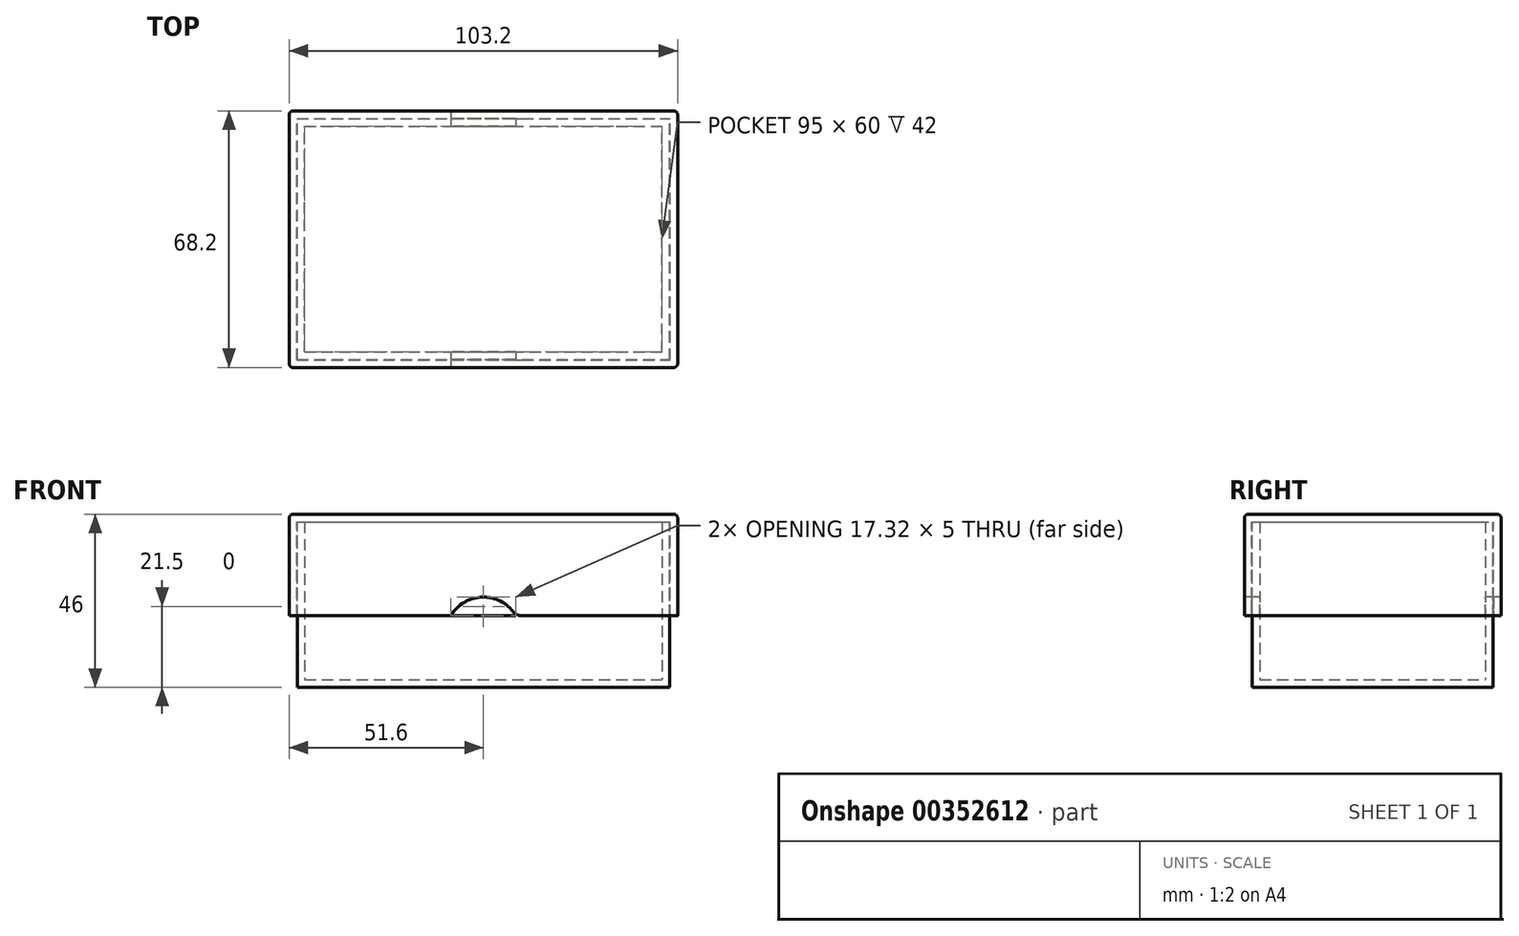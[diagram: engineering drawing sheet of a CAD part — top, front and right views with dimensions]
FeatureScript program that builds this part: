
annotation { "Feature Type Name" : "Feature", "Feature Type Description" : "" }
export const myFeature = defineFeature(function(context is Context, id is Id, definition is map)
    precondition{}
    {
        {
            var Q0;
            Q0=qCreatedBy(makeId("Top.planeOp"),FACE);
            var sketch = newSketch(context, id + "F0", { "sketchPlane" : qUnion([Q0])});
            skLineSegment(sketch, "E0.bottom", {"start": v(0, 0) * mm, "end": v(95, 0) * mm});
            skLineSegment(sketch, "E0.top", {"start": v(0, 60) * mm, "end": v(95, 60) * mm});
            skLineSegment(sketch, "E0.left", {"start": v(0, 0) * mm, "end": v(0, 60) * mm});
            skLineSegment(sketch, "E0.right", {"start": v(95, 0) * mm, "end": v(95, 60) * mm});
            skLineSegment(sketch, "E1.0", {"start": v(-2, 62) * mm, "end": v(97, 62) * mm});
            skLineSegment(sketch, "E1.1", {"start": v(-2, -2) * mm, "end": v(-2, 62) * mm});
            skLineSegment(sketch, "E1.2", {"start": v(-2, -2) * mm, "end": v(97, -2) * mm});
            skLineSegment(sketch, "E1.3", {"start": v(97, -2) * mm, "end": v(97, 62) * mm});
            skSolve(sketch);
        }
        {
            var Q0;
            Q0=makeQuery(id+"F0.imprint","IMPRINT",FACE,{"disambiguationData":[TD([[makeQuery(id+"F0.imprint","IMPRINT",EDGE,{"derivedFrom":sQuery(id+"F0.wireOp",EDGE,"E0.bottom")}),1.0]])]});
            var Q1;
            Q1=makeQuery(id+"F0.imprint","IMPRINT",FACE,{"disambiguationData":[TD([[makeQuery(id+"F0.imprint","IMPRINT",EDGE,{"derivedFrom":sQuery(id+"F0.wireOp",EDGE,"E0.bottom")}),-1.0]])]});
            extrude(context, id + "F1", {"entities" : qUnion([Q0, Q1]), "oppositeDirection" : true, "depth" : 2 * mm});
        }
        {
            var Q0;
            Q0=makeQuery(id+"F0.imprint","IMPRINT",FACE,{"disambiguationData":[TD([[makeQuery(id+"F0.imprint","IMPRINT",EDGE,{"derivedFrom":sQuery(id+"F0.wireOp",EDGE,"E0.bottom")}),-1.0]])]});
            extrude(context, id + "F2", {"entities" : qUnion([Q0]), "operationType" : NewBodyOperationType.ADD, "depth" : 42 * mm});
        }
        {
            var Q0;
            Q0=makeQuery(id+"F2.opExtrude","CAP_FACE",FACE,{"disambiguationData":[OSD([sQuery(id+"F0.wireOp",EDGE,"E0.bottom"),sQuery(id+"F0.wireOp",EDGE,"E0.top"),sQuery(id+"F0.wireOp",EDGE,"E0.left"),sQuery(id+"F0.wireOp",EDGE,"E0.right"),sQuery(id+"F0.wireOp",EDGE,"E1.0"),sQuery(id+"F0.wireOp",EDGE,"E1.1"),sQuery(id+"F0.wireOp",EDGE,"E1.2"),sQuery(id+"F0.wireOp",EDGE,"E1.3")])],"isStart":false});
            var sketch = newSketch(context, id + "F3", { "sketchPlane" : qUnion([Q0])});
            skLineSegment(sketch, "E2.0", {"start": v(-2, -2) * mm, "end": v(97, -2) * mm, "construction": true});
            skLineSegment(sketch, "E3.0", {"start": v(-2, -2) * mm, "end": v(-2, 62) * mm, "construction": true});
            skLineSegment(sketch, "E4.0", {"start": v(-2, 62) * mm, "end": v(97, 62) * mm, "construction": true});
            skLineSegment(sketch, "E5.0", {"start": v(97, -2) * mm, "end": v(97, 62) * mm, "construction": true});
            skLineSegment(sketch, "E6.0", {"start": v(-2.1, -2.1) * mm, "end": v(97.1, -2.1) * mm});
            skLineSegment(sketch, "E6.1", {"start": v(-2.1, -2.1) * mm, "end": v(-2.1, 62.1) * mm});
            skLineSegment(sketch, "E6.2", {"start": v(-2.1, 62.1) * mm, "end": v(97.1, 62.1) * mm});
            skLineSegment(sketch, "E6.3", {"start": v(97.1, -2.1) * mm, "end": v(97.1, 62.1) * mm});
            skLineSegment(sketch, "E7.0", {"start": v(-4.1, -4.1) * mm, "end": v(99.1, -4.1) * mm});
            skLineSegment(sketch, "E7.1", {"start": v(-4.1, -4.1) * mm, "end": v(-4.1, 64.1) * mm});
            skLineSegment(sketch, "E7.2", {"start": v(-4.1, 64.1) * mm, "end": v(99.1, 64.1) * mm});
            skLineSegment(sketch, "E7.3", {"start": v(99.1, -4.1) * mm, "end": v(99.1, 64.1) * mm});
            skSolve(sketch);
        }
        {
            var Q0;
            Q0=makeQuery(id+"F3.imprint","IMPRINT",FACE,{"disambiguationData":[TD([[makeQuery(id+"F3.imprint","IMPRINT",EDGE,{"derivedFrom":makeQuery(id+"F2.opExtrude","CAP_EDGE",EDGE,{"disambiguationData":[OSD([sQuery(id+"F0.wireOp",EDGE,"E0.bottom")])],"isStart":false})}),1.0]])]});
            var Q1;
            Q1=makeQuery(id+"F3.imprint","IMPRINT",FACE,{"disambiguationData":[TD([[makeQuery(id+"F3.imprint","IMPRINT",EDGE,{"derivedFrom":makeQuery(id+"F2.opExtrude","CAP_EDGE",EDGE,{"disambiguationData":[OSD([sQuery(id+"F0.wireOp",EDGE,"E0.bottom")])],"isStart":false})}),-1.0]])]});
            var Q2;
            Q2=makeQuery(id+"F3.imprint","IMPRINT",FACE,{"disambiguationData":[TD([[makeQuery(id+"F3.imprint","IMPRINT",EDGE,{"derivedFrom":sQuery(id+"F3.wireOp",EDGE,"E6.0")}),1.0]])]});
            var Q3;
            Q3=makeQuery(id+"F3.imprint","IMPRINT",FACE,{"disambiguationData":[TD([[makeQuery(id+"F3.imprint","IMPRINT",EDGE,{"derivedFrom":sQuery(id+"F3.wireOp",EDGE,"E6.0")}),-1.0]])]});
            extrude(context, id + "F4", {"entities" : qUnion([Q0, Q1, Q2, Q3]), "depth" : 2 * mm});
        }
        {
            var Q0;
            Q0=makeQuery(id+"F3.imprint","IMPRINT",FACE,{"disambiguationData":[TD([[makeQuery(id+"F3.imprint","IMPRINT",EDGE,{"derivedFrom":sQuery(id+"F3.wireOp",EDGE,"E6.0")}),-1.0]])]});
            extrude(context, id + "F5", {"entities" : qUnion([Q0]), "operationType" : NewBodyOperationType.ADD, "oppositeDirection" : true, "depth" : 25 * mm});
        }
        {
            var Q0;
            {var subQ0=sQuery(id+"F3.wireOp",EDGE,"E7.0");Q0=makeQuery(id+"F5.boolean.opBoolean","MERGE",FACE,{"derivedFrom":[makeQuery(id+"F4.opExtrude","SWEPT_FACE",FACE,{"disambiguationData":[OSD([subQ0])]}),makeQuery(id+"F5.opExtrude","SWEPT_FACE",FACE,{"disambiguationData":[OSD([subQ0])]})]});}
            var sketch = newSketch(context, id + "F6", { "sketchPlane" : qUnion([Q0])});
            skCircle(sketch, "E8", {"center": v(47.5, 12) * mm, "radius": 10 * mm});
            skPoint(sketch, "E8.first.point", {"position": v(38.84, 17) * mm});
            skPoint(sketch, "E8.second.point", {"position": v(47.5, 22) * mm});
            skPoint(sketch, "E8.second.point.positionSnap0", {"position": v(47.5, 17) * mm});
            skPoint(sketch, "E8.third.point", {"position": v(56.16, 17) * mm});
            skSolve(sketch);
        }
        {
            var Q0;
            {var subQ0=sQuery(id+"F6.wireOp",EDGE,"E8");var subQ1=makeQuery(id+"F5.opExtrude","CAP_EDGE",EDGE,{"disambiguationData":[OSD([sQuery(id+"F3.wireOp",EDGE,"E7.0")])],"isStart":false});var subQ2=makeQuery(id+"F6.imprint","INTERSECT",VERTEX,{"disambiguationData":[OD(0.0)],"derivedFrom":[subQ1,subQ0]});Q0=makeQuery(id+"F6.imprint","IMPRINT",FACE,{"disambiguationData":[TD([[makeQuery(id+"F6.imprint","IMPRINT",EDGE,{"disambiguationData":[TD([[subQ2,1.0]])],"derivedFrom":subQ0}),1.0]])]});}
            extrude(context, id + "F7", {"entities" : qUnion([Q0]), "operationType" : NewBodyOperationType.REMOVE, "endBound" : BoundingType.THROUGH_ALL, "oppositeDirection" : true, "depth" : 25 * mm});
        }
        {
            var Q0;
            {var subQ0=sQuery(id+"F3.wireOp",EDGE,"E7.0");var subQ2=sQuery(id+"F6.wireOp",EDGE,"E8");Q0=makeQuery(id+"F7.boolean.opBoolean","COPY",EDGE,{"disambiguationData":[TD([makeQuery(id+"F4.opExtrude","SWEPT_FACE",FACE,{"disambiguationData":[OSD([subQ0])]})])],"derivedFrom":makeQuery(id+"F7.opExtrude","SWEPT_EDGE",EDGE,{"disambiguationData":[OSD([subQ0,subQ2]),TDD([makeQuery(id+"F6.imprint","INTERSECT",VERTEX,{"disambiguationData":[OD(0.0)],"derivedFrom":[makeQuery(id+"F5.opExtrude","CAP_EDGE",EDGE,{"disambiguationData":[OSD([subQ0])],"isStart":false}),subQ2]})])]})});}
            var Q1;
            {var subQ0=sQuery(id+"F3.wireOp",EDGE,"E7.0");var subQ2=sQuery(id+"F6.wireOp",EDGE,"E8");Q1=makeQuery(id+"F7.boolean.opBoolean","COPY",EDGE,{"disambiguationData":[TD([makeQuery(id+"F4.opExtrude","SWEPT_FACE",FACE,{"disambiguationData":[OSD([subQ0])]})])],"derivedFrom":makeQuery(id+"F7.opExtrude","SWEPT_EDGE",EDGE,{"disambiguationData":[OSD([subQ0,subQ2]),TDD([makeQuery(id+"F6.imprint","INTERSECT",VERTEX,{"disambiguationData":[OD(1.0)],"derivedFrom":[makeQuery(id+"F5.opExtrude","CAP_EDGE",EDGE,{"disambiguationData":[OSD([subQ0])],"isStart":false}),subQ2]})])]})});}
            var Q2;
            {var subQ1=sQuery(id+"F3.wireOp",EDGE,"E7.2");var subQ2=sQuery(id+"F3.wireOp",EDGE,"E7.0");var subQ3=sQuery(id+"F6.wireOp",EDGE,"E8");Q2=makeQuery(id+"F7.boolean.opBoolean","COPY",EDGE,{"disambiguationData":[TD([makeQuery(id+"F4.opExtrude","SWEPT_FACE",FACE,{"disambiguationData":[OSD([subQ1])]})])],"derivedFrom":makeQuery(id+"F7.opExtrude","SWEPT_EDGE",EDGE,{"disambiguationData":[OSD([subQ2,subQ3]),TDD([makeQuery(id+"F6.imprint","INTERSECT",VERTEX,{"disambiguationData":[OD(0.0)],"derivedFrom":[makeQuery(id+"F5.opExtrude","CAP_EDGE",EDGE,{"disambiguationData":[OSD([subQ2])],"isStart":false}),subQ3]})])]})});}
            var Q3;
            {var subQ1=sQuery(id+"F3.wireOp",EDGE,"E7.2");var subQ2=sQuery(id+"F3.wireOp",EDGE,"E7.0");var subQ3=sQuery(id+"F6.wireOp",EDGE,"E8");Q3=makeQuery(id+"F7.boolean.opBoolean","COPY",EDGE,{"disambiguationData":[TD([makeQuery(id+"F4.opExtrude","SWEPT_FACE",FACE,{"disambiguationData":[OSD([subQ1])]})])],"derivedFrom":makeQuery(id+"F7.opExtrude","SWEPT_EDGE",EDGE,{"disambiguationData":[OSD([subQ2,subQ3]),TDD([makeQuery(id+"F6.imprint","INTERSECT",VERTEX,{"disambiguationData":[OD(1.0)],"derivedFrom":[makeQuery(id+"F5.opExtrude","CAP_EDGE",EDGE,{"disambiguationData":[OSD([subQ2])],"isStart":false}),subQ3]})])]})});}
            fillet(context, id + "F8", {"entities" : qUnion([Q0, Q1, Q2, Q3]), "radius" : 3 * mm, "tangentPropagation" : true, "allowEdgeOverflow" : false});
        }
        {
            var Q0;
            Q0=makeQuery(id+"F4.opExtrude","CAP_FACE",FACE,{"disambiguationData":[OSD([sQuery(id+"F3.wireOp",EDGE,"E7.0"),sQuery(id+"F3.wireOp",EDGE,"E7.1"),sQuery(id+"F3.wireOp",EDGE,"E7.2"),sQuery(id+"F3.wireOp",EDGE,"E7.3")])],"isStart":false});
            var Q1;
            {var subQ0=sQuery(id+"F3.wireOp",EDGE,"E7.3");var subQ1=sQuery(id+"F3.wireOp",EDGE,"E7.0");Q1=makeQuery(id+"F5.boolean.opBoolean","MERGE",EDGE,{"derivedFrom":[makeQuery(id+"F4.opExtrude","SWEPT_EDGE",EDGE,{"disambiguationData":[OSD([subQ1,subQ0])]}),makeQuery(id+"F5.opExtrude","SWEPT_EDGE",EDGE,{"disambiguationData":[OSD([subQ1,subQ0])]})]});}
            var Q2;
            {var subQ0=sQuery(id+"F3.wireOp",EDGE,"E7.3");var subQ1=sQuery(id+"F3.wireOp",EDGE,"E7.2");Q2=makeQuery(id+"F5.boolean.opBoolean","MERGE",EDGE,{"derivedFrom":[makeQuery(id+"F4.opExtrude","SWEPT_EDGE",EDGE,{"disambiguationData":[OSD([subQ1,subQ0])]}),makeQuery(id+"F5.opExtrude","SWEPT_EDGE",EDGE,{"disambiguationData":[OSD([subQ1,subQ0])]})]});}
            var Q3;
            {var subQ0=sQuery(id+"F3.wireOp",EDGE,"E7.2");var subQ1=sQuery(id+"F3.wireOp",EDGE,"E7.1");Q3=makeQuery(id+"F5.boolean.opBoolean","MERGE",EDGE,{"derivedFrom":[makeQuery(id+"F4.opExtrude","SWEPT_EDGE",EDGE,{"disambiguationData":[OSD([subQ1,subQ0])]}),makeQuery(id+"F5.opExtrude","SWEPT_EDGE",EDGE,{"disambiguationData":[OSD([subQ1,subQ0])]})]});}
            var Q4;
            {var subQ0=sQuery(id+"F3.wireOp",EDGE,"E7.1");var subQ1=sQuery(id+"F3.wireOp",EDGE,"E7.0");Q4=makeQuery(id+"F5.boolean.opBoolean","MERGE",EDGE,{"derivedFrom":[makeQuery(id+"F4.opExtrude","SWEPT_EDGE",EDGE,{"disambiguationData":[OSD([subQ1,subQ0])]}),makeQuery(id+"F5.opExtrude","SWEPT_EDGE",EDGE,{"disambiguationData":[OSD([subQ1,subQ0])]})]});}
            fillet(context, id + "F9", {"entities" : qUnion([Q0, Q1, Q2, Q3, Q4]), "radius" : 1 * mm, "tangentPropagation" : true, "allowEdgeOverflow" : false});
        }
    });
